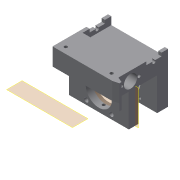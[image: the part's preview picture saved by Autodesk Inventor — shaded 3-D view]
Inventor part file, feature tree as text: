
AUTODESK INVENTOR PART (.ipt)
format: ipt  version: 2019.4 (Build 234330000, 330)  size: 347,136 bytes
history: native  units: mm
features: sketch x15, extrude x10, projected_geometry x10, hole x6, plane x4, other x3
ambient origin geometry x8: Origin, YZ Plane, XZ Plane, XY Plane, X Axis, Y Axis, Z Axis, Center Point
bodies: Body1 (feature_tree)
feature tree (48):
  plane  "Work Plane5"
  extrude  "Extrusion7"  Depth=16.0mm TaperAngle=0.0deg
  extrude  "Extrusion8"  Depth=24.0mm
  hole  "Hole1"  [1 undecoded]
  extrude  "Extrusion9"  Depth=6.2mm
  extrude  "Extrusion12"  Depth=10.0mm TaperAngle=0.0deg
  hole  "Hole4"  [1 undecoded]
  plane  "Work Plane8"
  extrude  "Extrusion13"  Depth=3.0mm
  extrude  "Extrusion18"  Depth=0.3mm
  extrude  "Extrusion19"  Depth=1.0mm
  extrude  "Extrusion20"  Depth=1.0mm
  hole  "Hole5"  [1 undecoded]
  hole  "Hole7"  [1 undecoded]
  hole  "Hole8"  [1 undecoded]
  sketch  "Sketch30"  dims[d122=6.9mm d123=2.0mm d124=0.0mm]
  plane  "Work Plane9"
  extrude  "Extrusion21"  Depth=8.0mm
  sketch  "Sketch31"  dims[d125=3.0mm d126=0.0mm]
  plane  "Work Plane10"
  extrude  "Extrusion22"  Depth=8.0mm
  hole  "Hole9"  [1 undecoded]
  sketch  "Sketch7"  dims[d33=16.0mm d34=0.0mm d41=16.0mm d42=0.0mm]
  sketch  "Sketch8"  dims[d43=2.9mm d44=6.0mm d45=4.0mm d46=2.0mm d47=90.0deg d48=4.0mm d49=20.594885mm d50=24.0mm]
  sketch  "Sketch9"  dims[d51=32.0mm d52=10.0mm d53=0.0mm]
  sketch  "Sketch10"  dims[d67=6.2mm d68=6.2mm]
  projected_geometry  "Projected Loop6"
  sketch  "Sketch17"  dims[d73=7.0mm d75=10.0mm d76=0.0mm]
  sketch  "Sketch18"  dims[d77=12.0mm]
  projected_geometry  "Projected Loop7"
  sketch  "Sketch23"  dims[d85=3.5mm d86=6.0mm d87=7.0mm d88=4.0mm d89=90.0deg d90=8.0mm d91=20.594885mm d92=20.0mm]
  projected_geometry  "Projected Loop12"
  sketch  "Sketch24"  dims[d93=6.0mm d94=3.0mm d95=0.0mm d96=0.0mm d112=47.0mm]
  sketch  "Sketch25"  dims[d113=0.1mm d114=0.3mm]
  projected_geometry  "Projected Loop13"
  sketch  "Sketch26"  dims[d115=4.0mm d116=1.0mm]
  sketch  "Sketch28"  dims[d117=1.0mm d118=1.0mm]
  projected_geometry  "Projected Loop16"
  sketch  "Sketch29"  dims[d119=3.0mm d120=0.0mm d121=3.0mm]
  projected_geometry  "Projected Loop17"
  projected_geometry  "Projected Loop18"
  projected_geometry  "Projected Loop19"
  projected_geometry  "Projected Loop20"
  sketch  "Sketch32"  dims[d127=2.8mm d128=6.0mm d129=19.05mm d130=4.775mm d131=90.0deg d132=8.0mm d133=20.594885mm d143=4.0mm d144=6.0mm d145=19.05mm d146=4.775mm d147=90.0deg d148=8.0mm d149=20.594885mm d150=2.8mm d151=2.8mm d152=45.0mm d153=25.0mm d154=2.8mm d155=6.0mm d156=19.05mm d157=4.775mm d158=90.0deg d159=8.0mm d160=20.594885mm d161=5.0mm d162=2.0mm d163=10.0mm d164=0.0mm d165=10.0mm d166=0.0mm d167=2.5mm d168=6.0mm d169=4.0mm d170=2.0mm d171=90.0deg d172=8.0mm d173=20.594885mm]
  projected_geometry  "Projected Loop21"
  other  "Assembly_Opentrons_Imagingunit_v0.iam"
  other  "Assembly_spindeldrive_350mm:1"
  other  "00_spindel_bearings:1"
note: 6 required parameter values undecoded (feature->parameter linkage not recoverable at this tier; creation-order binding heuristic only, values carry confidence <= 0.55)
